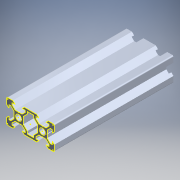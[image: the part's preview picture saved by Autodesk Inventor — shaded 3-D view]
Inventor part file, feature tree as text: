
AUTODESK INVENTOR PART (.ipt)
format: ipt  version: 2018 (Build 220112000, 112)  size: 253,440 bytes
history: native  units: mm
features: other x3, sketch x1
ambient origin geometry x8: Origin, YZ Plane, XZ Plane, XY Plane, X Axis, Y Axis, Z Axis, Center Point
bodies: Body1 (feature_tree)
feature tree (4):
  other  "Sólido1"
  sketch  "Esboço1"
  other  "Contorno projetado1"
  other  "Retangular PF20-12 - PERFIL 2040 V-SLOT(1)"
